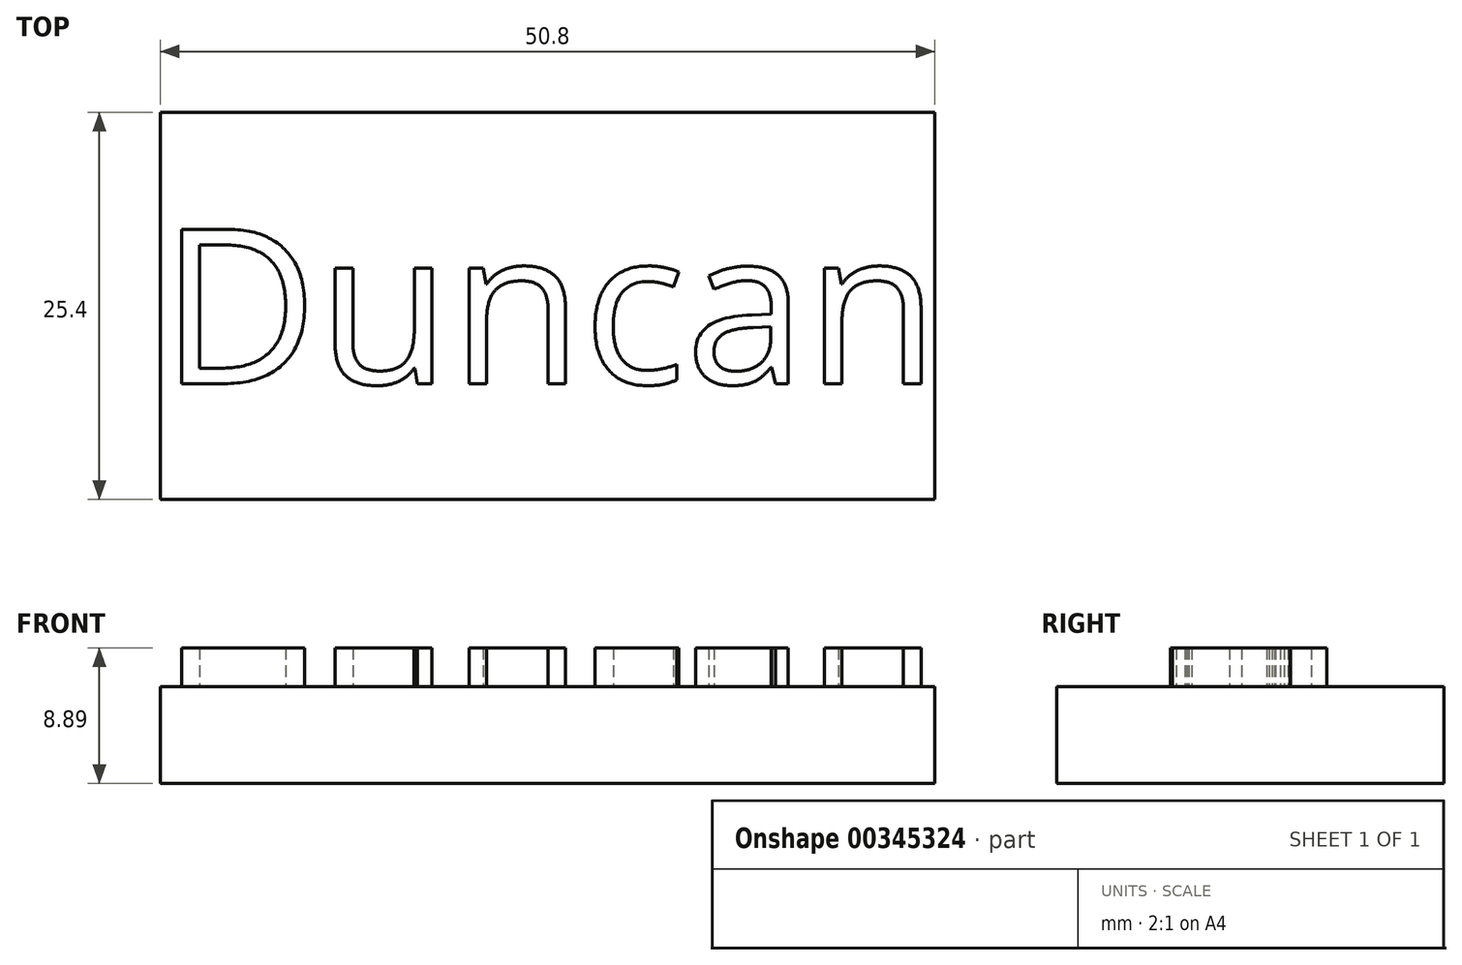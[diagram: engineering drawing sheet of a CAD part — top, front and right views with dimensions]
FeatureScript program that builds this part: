
annotation { "Feature Type Name" : "Feature", "Feature Type Description" : "" }
export const myFeature = defineFeature(function(context is Context, id is Id, definition is map)
    precondition{}
    {
        {
            var Q0;
            Q0=qCreatedBy(makeId("Top.planeOp"),FACE);
            var sketch = newSketch(context, id + "F0", { "sketchPlane" : qUnion([Q0])});
            skLineSegment(sketch, "E0.bottom", {"start": v(-25.4, 12.7) * mm, "end": v(25.4, 12.7) * mm});
            skLineSegment(sketch, "E0.top", {"start": v(-25.4, -12.7) * mm, "end": v(25.4, -12.7) * mm});
            skLineSegment(sketch, "E0.left", {"start": v(-25.4, 12.7) * mm, "end": v(-25.4, -12.7) * mm});
            skLineSegment(sketch, "E0.right", {"start": v(25.4, 12.7) * mm, "end": v(25.4, -12.7) * mm});
            skSolve(sketch);
        }
        {
            var Q0;
            Q0 = qSketchRegion(id + "F0", true);
            extrude(context, id + "F1", {"entities" : qUnion([Q0]), "depth" : 6.35 * mm});
        }
        {
            var Q0;
            Q0=makeQuery(id+"F1.opExtrude","CAP_FACE",FACE,{"disambiguationData":[OSD([sQuery(id+"F0.wireOp",EDGE,"E0.bottom"),sQuery(id+"F0.wireOp",EDGE,"E0.top"),sQuery(id+"F0.wireOp",EDGE,"E0.left"),sQuery(id+"F0.wireOp",EDGE,"E0.right")])],"isStart":false});
            var sketch = newSketch(context, id + "F2", { "sketchPlane" : qUnion([Q0])});
            skText(sketch, "E1", { "text": "Duncan", "fontName": "OpenSans-Regular.ttf"});
            const initialGuessF2  = {"E1": [-0.0254, -0.0051, 1, 0, 0.0102]};
            skSetInitialGuess(sketch, initialGuessF2);
            skSolve(sketch);
        }
        {
            var Q0;
            Q0 = qSketchRegion(id + "F2", true);
            extrude(context, id + "F3", {"entities" : qUnion([Q0]), "operationType" : NewBodyOperationType.ADD, "depth" : 2.54 * mm});
        }
    });
